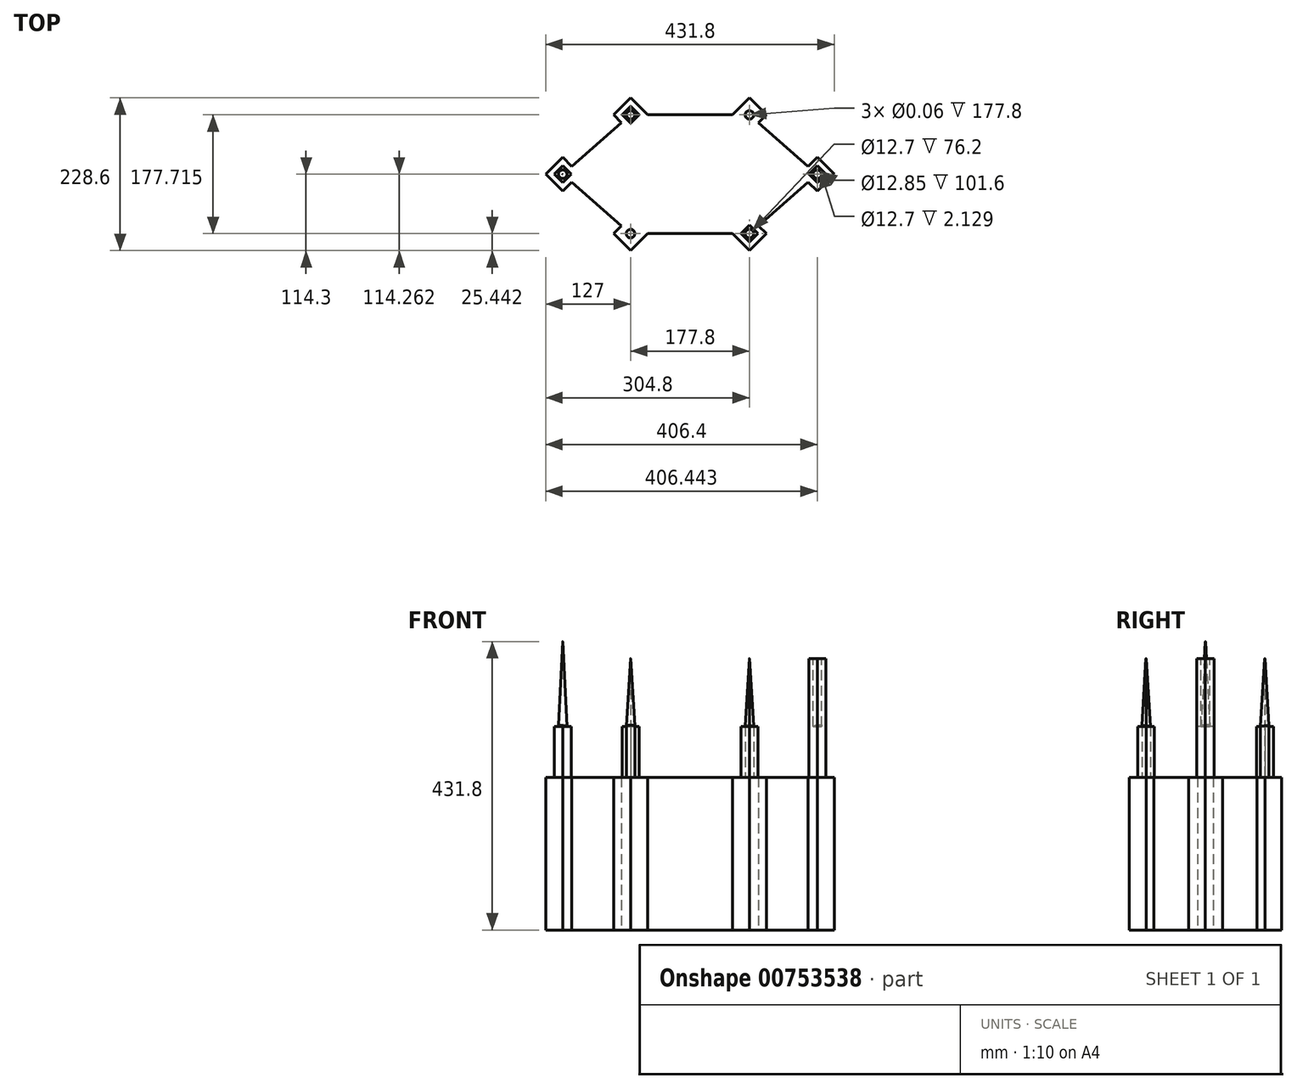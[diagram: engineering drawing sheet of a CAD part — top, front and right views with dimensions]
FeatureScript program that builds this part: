
annotation { "Feature Type Name" : "Feature", "Feature Type Description" : "" }
export const myFeature = defineFeature(function(context is Context, id is Id, definition is map)
    precondition{}
    {
        {
            var Q0;
            Q0=qCreatedBy(makeId("Top.planeOp"),FACE);
            var sketch = newSketch(context, id + "F0", { "sketchPlane" : qUnion([Q0])});
            skLineSegment(sketch, "E0", {"start": v(0, 88.9) * mm, "end": v(-63.5, 88.9) * mm});
            skLineSegment(sketch, "E1", {"start": v(-63.5, 88.9) * mm, "end": v(-88.9, 114.3) * mm});
            skLineSegment(sketch, "E2", {"start": v(-88.9, 114.3) * mm, "end": v(-114.3, 88.9) * mm});
            skLineSegment(sketch, "E3", {"start": v(-114.3, 88.9) * mm, "end": v(-88.9, 63.5) * mm});
            skLineSegment(sketch, "E4", {"start": v(-88.9, 63.5) * mm, "end": v(-63.5, 88.9) * mm});
            skLineSegment(sketch, "E5", {"start": v(-88.9, 63.5) * mm, "end": v(-88.9, 0) * mm});
            skLineSegment(sketch, "E6", {"start": v(-88.9, 88.9) * mm, "end": v(-190.5, 0) * mm});
            skLineSegment(sketch, "E7", {"start": v(-88.9, 114.3) * mm, "end": v(-88.9, 63.5) * mm, "construction": true});
            skLineSegment(sketch, "E8", {"start": v(-63.5, 88.9) * mm, "end": v(-114.3, 88.9) * mm, "construction": true});
            skLineSegment(sketch, "E9", {"start": v(-190.5, 25.4) * mm, "end": v(-215.9, 0) * mm});
            skLineSegment(sketch, "E10", {"start": v(-190.5, 25.4) * mm, "end": v(-165.1, 0) * mm});
            skLineSegment(sketch, "E11", {"start": v(-190.5, 25.4) * mm, "end": v(-190.5, 0) * mm, "construction": true});
            skPoint(sketch, "E12", {"position": v(-190.5, 0) * mm});
            skLineSegment(sketch, "E13.MirrorCS", {"start": v(-114.3, -88.9) * mm, "end": v(-88.9, -63.5) * mm});
            skLineSegment(sketch, "E14.MirrorCS", {"start": v(-88.9, -63.5) * mm, "end": v(-63.5, -88.9) * mm});
            skLineSegment(sketch, "E15.MirrorCS", {"start": v(-63.5, -88.9) * mm, "end": v(-114.3, -88.9) * mm, "construction": true});
            skLineSegment(sketch, "E16.MirrorCS", {"start": v(-190.5, -25.4) * mm, "end": v(-165.1, 0) * mm});
            skLineSegment(sketch, "E17.MirrorCS", {"start": v(-63.5, -88.9) * mm, "end": v(-88.9, -114.3) * mm});
            skLineSegment(sketch, "E18.MirrorCS", {"start": v(-88.9, -114.3) * mm, "end": v(-88.9, -63.5) * mm, "construction": true});
            skLineSegment(sketch, "E19.MirrorCS", {"start": v(0, -88.9) * mm, "end": v(-63.5, -88.9) * mm});
            skLineSegment(sketch, "E20.MirrorCS", {"start": v(-88.9, -114.3) * mm, "end": v(-114.3, -88.9) * mm});
            skLineSegment(sketch, "E21.MirrorCS", {"start": v(-190.5, -25.4) * mm, "end": v(-215.9, 0) * mm});
            skLineSegment(sketch, "E22.MirrorCS", {"start": v(-88.9, -88.9) * mm, "end": v(-190.5, 0) * mm});
            skLineSegment(sketch, "E23.MirrorCS", {"start": v(-190.5, -25.4) * mm, "end": v(-190.5, 0) * mm, "construction": true});
            skLineSegment(sketch, "E24.MirrorCS", {"start": v(-88.9, -63.5) * mm, "end": v(-88.9, 0) * mm});
            skPoint(sketch, "E25.MirrorP", {"position": v(190.5, 0) * mm});
            skLineSegment(sketch, "E26.MirrorCS", {"start": v(63.5, 88.9) * mm, "end": v(114.3, 88.9) * mm, "construction": true});
            skLineSegment(sketch, "E27.MirrorCS", {"start": v(190.5, 25.4) * mm, "end": v(215.9, 0) * mm});
            skLineSegment(sketch, "E28.MirrorCS", {"start": v(63.5, -88.9) * mm, "end": v(114.3, -88.9) * mm, "construction": true});
            skLineSegment(sketch, "E29.MirrorCS", {"start": v(88.9, -63.5) * mm, "end": v(63.5, -88.9) * mm});
            skLineSegment(sketch, "E30.MirrorCS", {"start": v(190.5, 25.4) * mm, "end": v(165.1, 0) * mm});
            skLineSegment(sketch, "E31.MirrorCS", {"start": v(190.5, 25.4) * mm, "end": v(190.5, 0) * mm, "construction": true});
            skLineSegment(sketch, "E32.MirrorCS", {"start": v(114.3, -88.9) * mm, "end": v(88.9, -63.5) * mm});
            skLineSegment(sketch, "E33.MirrorCS", {"start": v(88.9, -63.5) * mm, "end": v(88.9, 0) * mm});
            skLineSegment(sketch, "E34.MirrorCS", {"start": v(190.5, -25.4) * mm, "end": v(190.5, 0) * mm, "construction": true});
            skLineSegment(sketch, "E35.MirrorCS", {"start": v(190.5, -25.4) * mm, "end": v(215.9, 0) * mm});
            skLineSegment(sketch, "E36.MirrorCS", {"start": v(190.5, -25.4) * mm, "end": v(165.1, 0) * mm});
            skLineSegment(sketch, "E37.MirrorCS", {"start": v(0, 88.9) * mm, "end": v(63.5, 88.9) * mm});
            skLineSegment(sketch, "E38.MirrorCS", {"start": v(114.3, 88.9) * mm, "end": v(88.9, 63.5) * mm});
            skLineSegment(sketch, "E39.MirrorCS", {"start": v(88.9, 63.5) * mm, "end": v(63.5, 88.9) * mm});
            skLineSegment(sketch, "E40.MirrorCS", {"start": v(88.9, -88.9) * mm, "end": v(190.5, 0) * mm});
            skLineSegment(sketch, "E41.MirrorCS", {"start": v(88.9, 114.3) * mm, "end": v(88.9, 63.5) * mm, "construction": true});
            skLineSegment(sketch, "E42.MirrorCS", {"start": v(0, -88.9) * mm, "end": v(63.5, -88.9) * mm});
            skLineSegment(sketch, "E43.MirrorCS", {"start": v(63.5, 88.9) * mm, "end": v(88.9, 114.3) * mm});
            skLineSegment(sketch, "E44.MirrorCS", {"start": v(88.9, 114.3) * mm, "end": v(114.3, 88.9) * mm});
            skLineSegment(sketch, "E45.MirrorCS", {"start": v(63.5, -88.9) * mm, "end": v(88.9, -114.3) * mm});
            skLineSegment(sketch, "E46.MirrorCS", {"start": v(88.9, 88.9) * mm, "end": v(190.5, 0) * mm});
            skLineSegment(sketch, "E47.MirrorCS", {"start": v(88.9, -114.3) * mm, "end": v(114.3, -88.9) * mm});
            skLineSegment(sketch, "E48.MirrorCS", {"start": v(88.9, 63.5) * mm, "end": v(88.9, 0) * mm});
            skLineSegment(sketch, "E49.MirrorCS", {"start": v(88.9, -114.3) * mm, "end": v(88.9, -63.5) * mm, "construction": true});
            skSolve(sketch);
        }
        {
            var Q0;
            {var subQ5=sQuery(id+"F0.wireOp",EDGE,"E9");Q0=makeQuery(id+"F0.imprint","IMPRINT",FACE,{"disambiguationData":[TD([[makeQuery(id+"F0.imprint","IMPRINT",EDGE,{"derivedFrom":subQ5}),1.0]])]});}
            var Q1;
            {var subQ0=sQuery(id+"F0.wireOp",EDGE,"E22.MirrorCS");var subQ1=sQuery(id+"F0.wireOp",EDGE,"E6");var subQ2=makeQuery(id+"F0.imprint","INTERSECT",VERTEX,{"derivedFrom":[subQ1,subQ0]});Q1=makeQuery(id+"F0.imprint","IMPRINT",FACE,{"disambiguationData":[TD([[makeQuery(id+"F0.imprint","IMPRINT",EDGE,{"disambiguationData":[TD([[subQ2,1.0]])],"derivedFrom":subQ1}),1.0]])]});}
            var Q2;
            {var subQ7=sQuery(id+"F0.wireOp",EDGE,"E5");Q2=makeQuery(id+"F0.imprint","IMPRINT",FACE,{"disambiguationData":[TD([[makeQuery(id+"F0.imprint","IMPRINT",EDGE,{"derivedFrom":subQ7}),-1.0]])]});}
            var Q3;
            Q3=makeQuery(id+"F0.imprint","IMPRINT",FACE,{"disambiguationData":[TD([[makeQuery(id+"F0.imprint","IMPRINT",EDGE,{"derivedFrom":sQuery(id+"F0.wireOp",EDGE,"E1")}),1.0]])]});
            var Q4;
            {var subQ0=sQuery(id+"F0.wireOp",EDGE,"E14.MirrorCS");Q4=makeQuery(id+"F0.imprint","IMPRINT",FACE,{"disambiguationData":[TD([[makeQuery(id+"F0.imprint","IMPRINT",EDGE,{"derivedFrom":subQ0}),-1.0]])]});}
            var Q5;
            {var subQ1=sQuery(id+"F0.wireOp",EDGE,"E29.MirrorCS");Q5=makeQuery(id+"F0.imprint","IMPRINT",FACE,{"disambiguationData":[TD([[makeQuery(id+"F0.imprint","IMPRINT",EDGE,{"derivedFrom":subQ1}),1.0]])]});}
            var Q6;
            {var subQ9=sQuery(id+"F0.wireOp",EDGE,"E33.MirrorCS");Q6=makeQuery(id+"F0.imprint","IMPRINT",FACE,{"disambiguationData":[TD([[makeQuery(id+"F0.imprint","IMPRINT",EDGE,{"derivedFrom":subQ9}),-1.0]])]});}
            var Q7;
            Q7=makeQuery(id+"F0.imprint","IMPRINT",FACE,{"disambiguationData":[TD([[makeQuery(id+"F0.imprint","IMPRINT",EDGE,{"derivedFrom":sQuery(id+"F0.wireOp",EDGE,"E0")}),1.0]])]});
            var Q8;
            {var subQ0=sQuery(id+"F0.wireOp",EDGE,"E39.MirrorCS");Q8=makeQuery(id+"F0.imprint","IMPRINT",FACE,{"disambiguationData":[TD([[makeQuery(id+"F0.imprint","IMPRINT",EDGE,{"derivedFrom":subQ0}),-1.0]])]});}
            var Q9;
            {var subQ5=sQuery(id+"F0.wireOp",EDGE,"E27.MirrorCS");Q9=makeQuery(id+"F0.imprint","IMPRINT",FACE,{"disambiguationData":[TD([[makeQuery(id+"F0.imprint","IMPRINT",EDGE,{"derivedFrom":subQ5}),-1.0]])]});}
            var Q10;
            {var subQ0=sQuery(id+"F0.wireOp",EDGE,"E36.MirrorCS");var subQ1=sQuery(id+"F0.wireOp",EDGE,"E30.MirrorCS");var subQ2=makeQuery(id+"F0.imprint","INTERSECT",VERTEX,{"derivedFrom":[subQ1,subQ0]});Q10=makeQuery(id+"F0.imprint","IMPRINT",FACE,{"disambiguationData":[TD([[makeQuery(id+"F0.imprint","IMPRINT",EDGE,{"disambiguationData":[TD([[subQ2,1.0]])],"derivedFrom":subQ1}),1.0]])]});}
            extrude(context, id + "F1", {"entities" : qUnion([Q0, Q1, Q2, Q3, Q4, Q5, Q6, Q7, Q8, Q9, Q10]), "depth" : 228.6 * mm, "offsetDistance" : 25.4 * mm});
        }
        {
            var Q0;
            Q0=makeQuery(id+"F1.opExtrude","CAP_FACE",FACE,{"disambiguationData":[OSD([sQuery(id+"F0.wireOp",EDGE,"E0"),sQuery(id+"F0.wireOp",EDGE,"E1"),sQuery(id+"F0.wireOp",EDGE,"E2"),sQuery(id+"F0.wireOp",EDGE,"E3"),sQuery(id+"F0.wireOp",EDGE,"E6"),sQuery(id+"F0.wireOp",EDGE,"E9"),sQuery(id+"F0.wireOp",EDGE,"E10"),sQuery(id+"F0.wireOp",EDGE,"E13.MirrorCS"),sQuery(id+"F0.wireOp",EDGE,"E16.MirrorCS"),sQuery(id+"F0.wireOp",EDGE,"E17.MirrorCS"),sQuery(id+"F0.wireOp",EDGE,"E19.MirrorCS"),sQuery(id+"F0.wireOp",EDGE,"E20.MirrorCS"),sQuery(id+"F0.wireOp",EDGE,"E21.MirrorCS"),sQuery(id+"F0.wireOp",EDGE,"E22.MirrorCS"),sQuery(id+"F0.wireOp",EDGE,"E27.MirrorCS"),sQuery(id+"F0.wireOp",EDGE,"E30.MirrorCS"),sQuery(id+"F0.wireOp",EDGE,"E32.MirrorCS"),sQuery(id+"F0.wireOp",EDGE,"E35.MirrorCS"),sQuery(id+"F0.wireOp",EDGE,"E36.MirrorCS"),sQuery(id+"F0.wireOp",EDGE,"E37.MirrorCS"),sQuery(id+"F0.wireOp",EDGE,"E38.MirrorCS"),sQuery(id+"F0.wireOp",EDGE,"E40.MirrorCS"),sQuery(id+"F0.wireOp",EDGE,"E42.MirrorCS"),sQuery(id+"F0.wireOp",EDGE,"E43.MirrorCS"),sQuery(id+"F0.wireOp",EDGE,"E44.MirrorCS"),sQuery(id+"F0.wireOp",EDGE,"E45.MirrorCS"),sQuery(id+"F0.wireOp",EDGE,"E46.MirrorCS"),sQuery(id+"F0.wireOp",EDGE,"E47.MirrorCS")])],"isStart":false});
            var sketch = newSketch(context, id + "F2", { "sketchPlane" : qUnion([Q0])});
            skLineSegment(sketch, "E50", {"start": v(-101.6, 88.9) * mm, "end": v(-88.9, 76.2) * mm});
            skLineSegment(sketch, "E51", {"start": v(-88.9, 76.2) * mm, "end": v(-76.2, 88.9) * mm});
            skLineSegment(sketch, "E52", {"start": v(-76.2, 88.9) * mm, "end": v(-88.9, 101.6) * mm});
            skLineSegment(sketch, "E53", {"start": v(-88.9, 101.6) * mm, "end": v(-101.6, 88.9) * mm});
            skCircle(sketch, "E54", {"center": v(-88.9, 88.86) * mm, "radius": 6.35 * mm});
            skCircle(sketch, "E55", {"center": v(-88.9, 88.86) * mm, "radius": 0.03 * mm});
            skCircle(sketch, "E56.MirrorC", {"center": v(-88.9, -88.86) * mm, "radius": 0.03 * mm});
            skCircle(sketch, "E57.MirrorC", {"center": v(-88.9, -88.86) * mm, "radius": 6.35 * mm});
            skLineSegment(sketch, "E58.MirrorCS", {"start": v(-88.9, -101.6) * mm, "end": v(-101.6, -88.9) * mm});
            skLineSegment(sketch, "E59.MirrorCS", {"start": v(-76.2, -88.9) * mm, "end": v(-88.9, -101.6) * mm});
            skLineSegment(sketch, "E60.MirrorCS", {"start": v(-88.9, -76.2) * mm, "end": v(-76.2, -88.9) * mm});
            skLineSegment(sketch, "E61.MirrorCS", {"start": v(-101.6, -88.9) * mm, "end": v(-88.9, -76.2) * mm});
            skCircle(sketch, "E62.MirrorC", {"center": v(88.9, 88.86) * mm, "radius": 0.03 * mm});
            skCircle(sketch, "E63.MirrorC", {"center": v(88.9, -88.86) * mm, "radius": 0.03 * mm});
            skCircle(sketch, "E64.MirrorC", {"center": v(88.9, 88.86) * mm, "radius": 6.35 * mm});
            skLineSegment(sketch, "E65.MirrorCS", {"start": v(88.9, 101.6) * mm, "end": v(101.6, 88.9) * mm});
            skLineSegment(sketch, "E66.MirrorCS", {"start": v(76.2, 88.9) * mm, "end": v(88.9, 101.6) * mm});
            skLineSegment(sketch, "E67.MirrorCS", {"start": v(88.9, 76.2) * mm, "end": v(76.2, 88.9) * mm});
            skLineSegment(sketch, "E68.MirrorCS", {"start": v(101.6, 88.9) * mm, "end": v(88.9, 76.2) * mm});
            skLineSegment(sketch, "E69.MirrorCS", {"start": v(101.6, -88.9) * mm, "end": v(88.9, -76.2) * mm});
            skLineSegment(sketch, "E70.MirrorCS", {"start": v(76.2, -88.9) * mm, "end": v(88.9, -101.6) * mm});
            skLineSegment(sketch, "E71.MirrorCS", {"start": v(88.9, -76.2) * mm, "end": v(76.2, -88.9) * mm});
            skCircle(sketch, "E72.MirrorC", {"center": v(88.9, -88.86) * mm, "radius": 6.35 * mm});
            skLineSegment(sketch, "E73.MirrorCS", {"start": v(88.9, -101.6) * mm, "end": v(101.6, -88.9) * mm});
            skLineSegment(sketch, "E74", {"start": v(-190.5, 12.7) * mm, "end": v(-203.2, 0) * mm});
            skLineSegment(sketch, "E75", {"start": v(-203.2, 0) * mm, "end": v(-190.5, -12.7) * mm});
            skLineSegment(sketch, "E76", {"start": v(-190.5, -12.7) * mm, "end": v(-177.8, 0) * mm});
            skLineSegment(sketch, "E77", {"start": v(-190.5, 12.7) * mm, "end": v(-177.8, 0) * mm});
            skCircle(sketch, "E78", {"center": v(-190.5, 0) * mm, "radius": 6.35 * mm});
            skCircle(sketch, "E79.MirrorC", {"center": v(190.5, 0) * mm, "radius": 6.35 * mm});
            skLineSegment(sketch, "E80.MirrorCS", {"start": v(203.2, 0) * mm, "end": v(190.5, -12.7) * mm});
            skLineSegment(sketch, "E81.MirrorCS", {"start": v(190.5, 12.7) * mm, "end": v(177.8, 0) * mm});
            skLineSegment(sketch, "E82.MirrorCS", {"start": v(190.5, -12.7) * mm, "end": v(177.8, 0) * mm});
            skLineSegment(sketch, "E83.MirrorCS", {"start": v(190.5, 12.7) * mm, "end": v(203.2, 0) * mm});
            skSolve(sketch);
        }
        {
            var Q0;
            Q0=makeQuery(id+"F2.imprint","IMPRINT",FACE,{"disambiguationData":[TD([[makeQuery(id+"F2.imprint","IMPRINT",EDGE,{"derivedFrom":sQuery(id+"F2.wireOp",EDGE,"E74")}),1.0]])]});
            var Q1;
            Q1=makeQuery(id+"F2.imprint","IMPRINT",FACE,{"disambiguationData":[TD([[makeQuery(id+"F2.imprint","IMPRINT",EDGE,{"derivedFrom":sQuery(id+"F2.wireOp",EDGE,"E50")}),1.0]])]});
            var Q2;
            Q2=makeQuery(id+"F2.imprint","IMPRINT",FACE,{"disambiguationData":[TD([[makeQuery(id+"F2.imprint","IMPRINT",EDGE,{"derivedFrom":sQuery(id+"F2.wireOp",EDGE,"E79.MirrorC")}),1.0]])]});
            var Q3;
            Q3=makeQuery(id+"F2.imprint","IMPRINT",FACE,{"disambiguationData":[TD([[makeQuery(id+"F2.imprint","IMPRINT",EDGE,{"derivedFrom":sQuery(id+"F2.wireOp",EDGE,"E69.MirrorCS")}),1.0]])]});
            var Q4;
            Q4=makeQuery(id+"F2.imprint","IMPRINT",FACE,{"disambiguationData":[TD([[makeQuery(id+"F2.imprint","IMPRINT",EDGE,{"derivedFrom":sQuery(id+"F2.wireOp",EDGE,"E57.MirrorC")}),1.0]])]});
            var Q5;
            Q5=makeQuery(id+"F2.imprint","IMPRINT",FACE,{"disambiguationData":[TD([[makeQuery(id+"F2.imprint","IMPRINT",EDGE,{"derivedFrom":sQuery(id+"F2.wireOp",EDGE,"E64.MirrorC")}),1.0]])]});
            extrude(context, id + "F3", {"entities" : qUnion([Q0, Q1, Q2, Q3, Q4, Q5]), "operationType" : NewBodyOperationType.ADD, "depth" : 76.2 * mm, "offsetDistance" : 25.4 * mm});
        }
        {
            var Q0;
            Q0=makeQuery(id+"F2.imprint","IMPRINT",FACE,{"disambiguationData":[TD([[makeQuery(id+"F2.imprint","IMPRINT",EDGE,{"derivedFrom":sQuery(id+"F2.wireOp",EDGE,"E54")}),1.0]])]});
            var Q1;
            Q1=makeQuery(id+"F2.imprint","IMPRINT",FACE,{"disambiguationData":[TD([[makeQuery(id+"F2.imprint","IMPRINT",EDGE,{"derivedFrom":sQuery(id+"F2.wireOp",EDGE,"E79.MirrorC")}),-1.0]])]});
            var Q2;
            Q2=makeQuery(id+"F2.imprint","IMPRINT",FACE,{"disambiguationData":[TD([[makeQuery(id+"F2.imprint","IMPRINT",EDGE,{"derivedFrom":sQuery(id+"F2.wireOp",EDGE,"E56.MirrorC")}),-1.0]])]});
            var Q3;
            Q3=makeQuery(id+"F2.imprint","IMPRINT",FACE,{"disambiguationData":[TD([[makeQuery(id+"F2.imprint","IMPRINT",EDGE,{"derivedFrom":sQuery(id+"F2.wireOp",EDGE,"E63.MirrorC")}),1.0]])]});
            var Q4;
            Q4=makeQuery(id+"F2.imprint","IMPRINT",FACE,{"disambiguationData":[TD([[makeQuery(id+"F2.imprint","IMPRINT",EDGE,{"derivedFrom":sQuery(id+"F2.wireOp",EDGE,"E62.MirrorC")}),-1.0]])]});
            extrude(context, id + "F4", {"entities" : qUnion([Q0, Q1, Q2, Q3, Q4]), "operationType" : NewBodyOperationType.ADD, "depth" : 177.8 * mm, "offsetDistance" : 25.4 * mm});
        }
        {
            var Q0;
            Q0=makeQuery(id+"F2.imprint","IMPRINT",FACE,{"disambiguationData":[TD([[makeQuery(id+"F2.imprint","IMPRINT",EDGE,{"derivedFrom":sQuery(id+"F2.wireOp",EDGE,"E78")}),1.0]])]});
            extrude(context, id + "F5", {"entities" : qUnion([Q0]), "operationType" : NewBodyOperationType.ADD, "depth" : 203.2 * mm, "offsetDistance" : 25.4 * mm});
        }
        {
            var Q0;
            Q0=makeQuery(id+"F1.opExtrude","SWEPT_FACE",FACE,{"disambiguationData":[OSD([sQuery(id+"F0.wireOp",EDGE,"E19.MirrorCS"),sQuery(id+"F0.wireOp",EDGE,"E42.MirrorCS")])]});
            var sketch = newSketch(context, id + "F6", { "sketchPlane" : qUnion([Q0])});
            skLineSegment(sketch, "E84.bottom", {"start": v(-88.9, 304.8) * mm, "end": v(-82.5, 304.8) * mm});
            skLineSegment(sketch, "E84.top", {"start": v(-88.9, 406.4) * mm, "end": v(-82.5, 406.4) * mm});
            skLineSegment(sketch, "E84.left", {"start": v(-88.9, 304.8) * mm, "end": v(-88.9, 406.4) * mm});
            skLineSegment(sketch, "E84.right", {"start": v(-82.5, 304.8) * mm, "end": v(-82.5, 406.4) * mm});
            skLineSegment(sketch, "E85", {"start": v(-88.87, 406.4) * mm, "end": v(-82.5, 304.8) * mm});
            skSolve(sketch);
        }
        {
            var Q0;
            {var subQ0=sQuery(id+"F6.wireOp",EDGE,"E84.right");Q0=makeQuery(id+"F6.imprint","IMPRINT",FACE,{"disambiguationData":[TD([[makeQuery(id+"F6.imprint","IMPRINT",EDGE,{"derivedFrom":subQ0}),1.0]])]});}
            var Q1;
            Q1=sQuery(id+"F6.wireOp",EDGE,"E84.left");
            revolve(context, id + "F7", {"operationType" : NewBodyOperationType.REMOVE, "surfaceOperationType" : NewSurfaceOperationType.NEW, "entities" : qUnion([Q0]), "axis" : qUnion([Q1]), "revolveType" : RevolveType.FULL, "oppositeDirection" : true});
        }
        {
            var Q0;
            Q0=makeQuery(id+"F1.opExtrude","SWEPT_FACE",FACE,{"disambiguationData":[OSD([sQuery(id+"F0.wireOp",EDGE,"E19.MirrorCS"),sQuery(id+"F0.wireOp",EDGE,"E42.MirrorCS")])]});
            var sketch = newSketch(context, id + "F8", { "sketchPlane" : qUnion([Q0])});
            skLineSegment(sketch, "E86.bottom", {"start": v(88.9, 304.8) * mm, "end": v(95.3, 304.8) * mm});
            skLineSegment(sketch, "E86.top", {"start": v(88.9, 406.4) * mm, "end": v(95.3, 406.4) * mm});
            skLineSegment(sketch, "E86.left", {"start": v(88.9, 304.8) * mm, "end": v(88.9, 406.4) * mm});
            skLineSegment(sketch, "E86.right", {"start": v(95.3, 304.8) * mm, "end": v(95.3, 406.4) * mm});
            skLineSegment(sketch, "E87", {"start": v(88.93, 406.4) * mm, "end": v(95.3, 304.8) * mm});
            skSolve(sketch);
        }
        {
            var Q0;
            {var subQ0=sQuery(id+"F8.wireOp",EDGE,"E86.right");Q0=makeQuery(id+"F8.imprint","IMPRINT",FACE,{"disambiguationData":[TD([[makeQuery(id+"F8.imprint","IMPRINT",EDGE,{"derivedFrom":subQ0}),1.0]])]});}
            var Q1;
            Q1=sQuery(id+"F8.wireOp",EDGE,"E86.left");
            revolve(context, id + "F9", {"operationType" : NewBodyOperationType.REMOVE, "surfaceOperationType" : NewSurfaceOperationType.NEW, "entities" : qUnion([Q0]), "axis" : qUnion([Q1]), "revolveType" : RevolveType.FULL, "oppositeDirection" : true});
        }
        {
            var Q0;
            Q0=makeQuery(id+"F1.opExtrude","SWEPT_FACE",FACE,{"disambiguationData":[OSD([sQuery(id+"F0.wireOp",EDGE,"E0"),sQuery(id+"F0.wireOp",EDGE,"E37.MirrorCS")])]});
            var sketch = newSketch(context, id + "F10", { "sketchPlane" : qUnion([Q0])});
            skLineSegment(sketch, "E88.bottom", {"start": v(88.9, 304.8) * mm, "end": v(95.3, 304.8) * mm});
            skLineSegment(sketch, "E88.top", {"start": v(88.9, 406.4) * mm, "end": v(95.3, 406.4) * mm});
            skLineSegment(sketch, "E88.left", {"start": v(88.9, 304.8) * mm, "end": v(88.9, 406.4) * mm});
            skLineSegment(sketch, "E88.right", {"start": v(95.3, 304.8) * mm, "end": v(95.3, 406.4) * mm});
            skLineSegment(sketch, "E89", {"start": v(88.93, 406.4) * mm, "end": v(95.3, 304.8) * mm});
            skSolve(sketch);
        }
        {
            var Q0;
            {var subQ0=sQuery(id+"F10.wireOp",EDGE,"E88.right");Q0=makeQuery(id+"F10.imprint","IMPRINT",FACE,{"disambiguationData":[TD([[makeQuery(id+"F10.imprint","IMPRINT",EDGE,{"derivedFrom":subQ0}),1.0]])]});}
            var Q1;
            Q1=sQuery(id+"F10.wireOp",EDGE,"E88.left");
            revolve(context, id + "F11", {"operationType" : NewBodyOperationType.REMOVE, "surfaceOperationType" : NewSurfaceOperationType.NEW, "entities" : qUnion([Q0]), "axis" : qUnion([Q1]), "revolveType" : RevolveType.FULL, "oppositeDirection" : true});
        }
        {
            var Q0;
            Q0=makeQuery(id+"F1.opExtrude","SWEPT_FACE",FACE,{"disambiguationData":[OSD([sQuery(id+"F0.wireOp",EDGE,"E0"),sQuery(id+"F0.wireOp",EDGE,"E37.MirrorCS")])]});
            var sketch = newSketch(context, id + "F12", { "sketchPlane" : qUnion([Q0])});
            skLineSegment(sketch, "E90.bottom", {"start": v(-82.5, 304.8) * mm, "end": v(-88.9, 304.8) * mm});
            skLineSegment(sketch, "E90.top", {"start": v(-82.5, 406.4) * mm, "end": v(-88.9, 406.4) * mm});
            skLineSegment(sketch, "E90.left", {"start": v(-82.5, 304.8) * mm, "end": v(-82.5, 406.4) * mm});
            skLineSegment(sketch, "E90.right", {"start": v(-88.9, 304.8) * mm, "end": v(-88.9, 406.4) * mm});
            skLineSegment(sketch, "E91", {"start": v(-88.87, 406.4) * mm, "end": v(-82.5, 304.8) * mm});
            skSolve(sketch);
        }
        {
            var Q0;
            {var subQ0=sQuery(id+"F12.wireOp",EDGE,"E90.left");Q0=makeQuery(id+"F12.imprint","IMPRINT",FACE,{"disambiguationData":[TD([[makeQuery(id+"F12.imprint","IMPRINT",EDGE,{"derivedFrom":subQ0}),1.0]])]});}
            var Q1;
            Q1=sQuery(id+"F12.wireOp",EDGE,"E90.right");
            revolve(context, id + "F13", {"operationType" : NewBodyOperationType.REMOVE, "surfaceOperationType" : NewSurfaceOperationType.NEW, "entities" : qUnion([Q0]), "axis" : qUnion([Q1]), "revolveType" : RevolveType.FULL, "oppositeDirection" : true});
        }
        {
            var Q0;
            Q0=makeQuery(id+"F1.opExtrude","SWEPT_FACE",FACE,{"disambiguationData":[OSD([sQuery(id+"F0.wireOp",EDGE,"E46.MirrorCS")])]});
            var sketch = newSketch(context, id + "F14", { "sketchPlane" : qUnion([Q0])});
            skLineSegment(sketch, "E92.bottom", {"start": v(-143.42, 304.8) * mm, "end": v(-137, 304.8) * mm});
            skLineSegment(sketch, "E92.top", {"start": v(-143.42, 406.4) * mm, "end": v(-137, 406.4) * mm});
            skLineSegment(sketch, "E92.left", {"start": v(-143.42, 304.8) * mm, "end": v(-143.42, 406.4) * mm});
            skLineSegment(sketch, "E92.right", {"start": v(-137, 304.8) * mm, "end": v(-137, 406.4) * mm});
            skLineSegment(sketch, "E93", {"start": v(-143.4, 406.4) * mm, "end": v(-137, 304.8) * mm});
            skSolve(sketch);
        }
        {
            var Q0;
            {var subQ0=sQuery(id+"F14.wireOp",EDGE,"E92.right");Q0=makeQuery(id+"F14.imprint","IMPRINT",FACE,{"disambiguationData":[TD([[makeQuery(id+"F14.imprint","IMPRINT",EDGE,{"derivedFrom":subQ0}),1.0]])]});}
            var Q1;
            Q1=sQuery(id+"F14.wireOp",EDGE,"E92.left");
            revolve(context, id + "F15", {"operationType" : NewBodyOperationType.REMOVE, "surfaceOperationType" : NewSurfaceOperationType.NEW, "entities" : qUnion([Q0]), "axis" : qUnion([Q1]), "revolveType" : RevolveType.FULL, "oppositeDirection" : true});
        }
        {
            var Q0;
            Q0=makeQuery(id+"F1.opExtrude","SWEPT_FACE",FACE,{"disambiguationData":[OSD([sQuery(id+"F0.wireOp",EDGE,"E22.MirrorCS")])]});
            var sketch = newSketch(context, id + "F16", { "sketchPlane" : qUnion([Q0])});
            skLineSegment(sketch, "E94.bottom", {"start": v(-143.42, 304.8) * mm, "end": v(-137, 304.8) * mm});
            skLineSegment(sketch, "E94.top", {"start": v(-143.42, 431.8) * mm, "end": v(-137, 431.8) * mm});
            skLineSegment(sketch, "E94.left", {"start": v(-143.42, 304.8) * mm, "end": v(-143.42, 431.8) * mm});
            skLineSegment(sketch, "E94.right", {"start": v(-137, 304.8) * mm, "end": v(-137, 431.8) * mm});
            skLineSegment(sketch, "E95", {"start": v(-143.4, 431.8) * mm, "end": v(-137, 304.8) * mm});
            skSolve(sketch);
        }
        {
            var Q0;
            {var subQ0=sQuery(id+"F16.wireOp",EDGE,"E94.right");Q0=makeQuery(id+"F16.imprint","IMPRINT",FACE,{"disambiguationData":[TD([[makeQuery(id+"F16.imprint","IMPRINT",EDGE,{"derivedFrom":subQ0}),1.0]])]});}
            var Q1;
            Q1=sQuery(id+"F16.wireOp",EDGE,"E94.left");
            revolve(context, id + "F17", {"operationType" : NewBodyOperationType.REMOVE, "surfaceOperationType" : NewSurfaceOperationType.NEW, "entities" : qUnion([Q0]), "axis" : qUnion([Q1]), "revolveType" : RevolveType.FULL, "oppositeDirection" : true});
        }
    });
